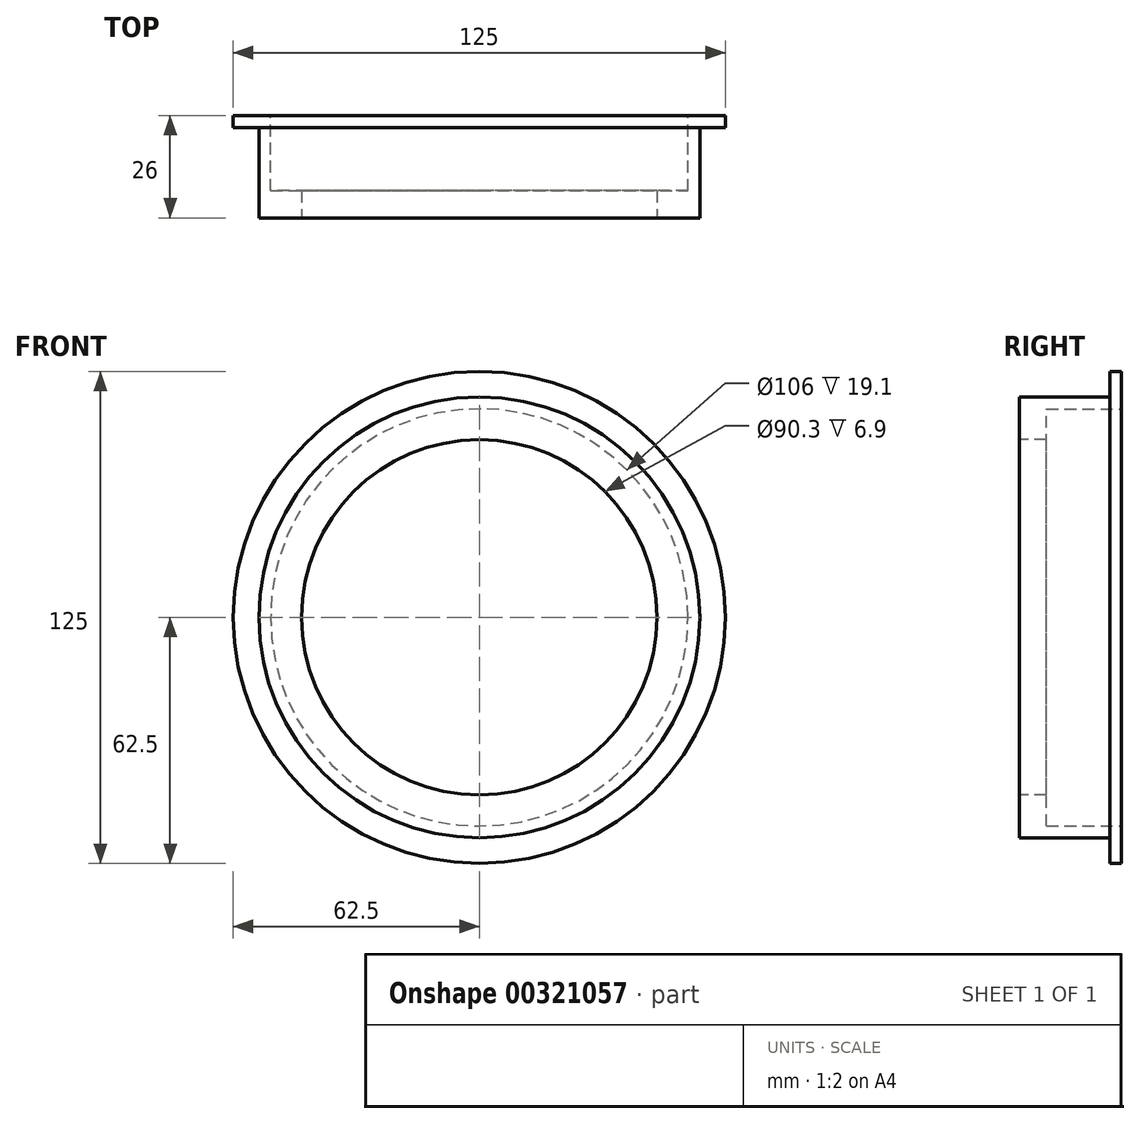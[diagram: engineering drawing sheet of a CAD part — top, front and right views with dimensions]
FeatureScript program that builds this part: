
annotation { "Feature Type Name" : "Feature", "Feature Type Description" : "" }
export const myFeature = defineFeature(function(context is Context, id is Id, definition is map)
    precondition{}
    {
        {
            var Q0;
            Q0=qCreatedBy(makeId("Front.planeOp"),FACE);
            var sketch = newSketch(context, id + "F0", { "sketchPlane" : qUnion([Q0])});
            skCircle(sketch, "E0", {"center": v(0, 0) * mm, "radius": 56 * mm});
            skCircle(sketch, "E1", {"center": v(0, 0) * mm, "radius": 53 * mm});
            skSolve(sketch);
        }
        {
            var Q0;
            Q0=qSketchRegion(id+"F0",true);
            extrude(context, id + "F1", {"entities" : qUnion([Q0]), "depth" : 20 * mm});
        }
        {
            var Q0;
            Q0=makeQuery(id+"F1.opExtrude","CAP_FACE",FACE,{"disambiguationData":[OSD([sQuery(id+"F0.wireOp",EDGE,"E0"),sQuery(id+"F0.wireOp",EDGE,"E1")])],"isStart":false});
            var sketch = newSketch(context, id + "F2", { "sketchPlane" : qUnion([Q0])});
            skCircle(sketch, "E2", {"center": v(0, 0) * mm, "radius": 56 * mm});
            skCircle(sketch, "E3", {"center": v(0, 0) * mm, "radius": 45.15 * mm});
            skSolve(sketch);
        }
        {
            var Q0;
            Q0=qSketchRegion(id+"F2",true);
            extrude(context, id + "F3", {"entities" : qUnion([Q0]), "operationType" : NewBodyOperationType.ADD, "oppositeDirection" : true, "depth" : 6.9 * mm});
        }
        {
            var Q0;
            Q0=makeQuery(id+"F1.opExtrude","CAP_FACE",FACE,{"disambiguationData":[OSD([sQuery(id+"F0.wireOp",EDGE,"E0"),sQuery(id+"F0.wireOp",EDGE,"E1")])],"isStart":true});
            var sketch = newSketch(context, id + "F4", { "sketchPlane" : qUnion([Q0])});
            skCircle(sketch, "E4", {"center": v(0, 0) * mm, "radius": 53 * mm});
            skCircle(sketch, "E5", {"center": v(0, 0) * mm, "radius": 56 * mm});
            skSolve(sketch);
        }
        {
            var Q0;
            Q0=qSketchRegion(id+"F4",true);
            extrude(context, id + "F5", {"entities" : qUnion([Q0]), "operationType" : NewBodyOperationType.ADD, "depth" : 3 * mm});
        }
        {
            var Q0;
            Q0=makeQuery(id+"F5.opExtrude","CAP_FACE",FACE,{"disambiguationData":[OSD([sQuery(id+"F4.wireOp",EDGE,"E4"),sQuery(id+"F4.wireOp",EDGE,"E5")])],"isStart":false});
            var sketch = newSketch(context, id + "F6", { "sketchPlane" : qUnion([Q0])});
            skCircle(sketch, "E6", {"center": v(0, 0) * mm, "radius": 53 * mm});
            skCircle(sketch, "E7", {"center": v(0, 0) * mm, "radius": 62.5 * mm});
            skSolve(sketch);
        }
        {
            var Q0;
            Q0=qSketchRegion(id+"F6",true);
            extrude(context, id + "F7", {"entities" : qUnion([Q0]), "operationType" : NewBodyOperationType.ADD, "depth" : 3 * mm});
        }
    });
